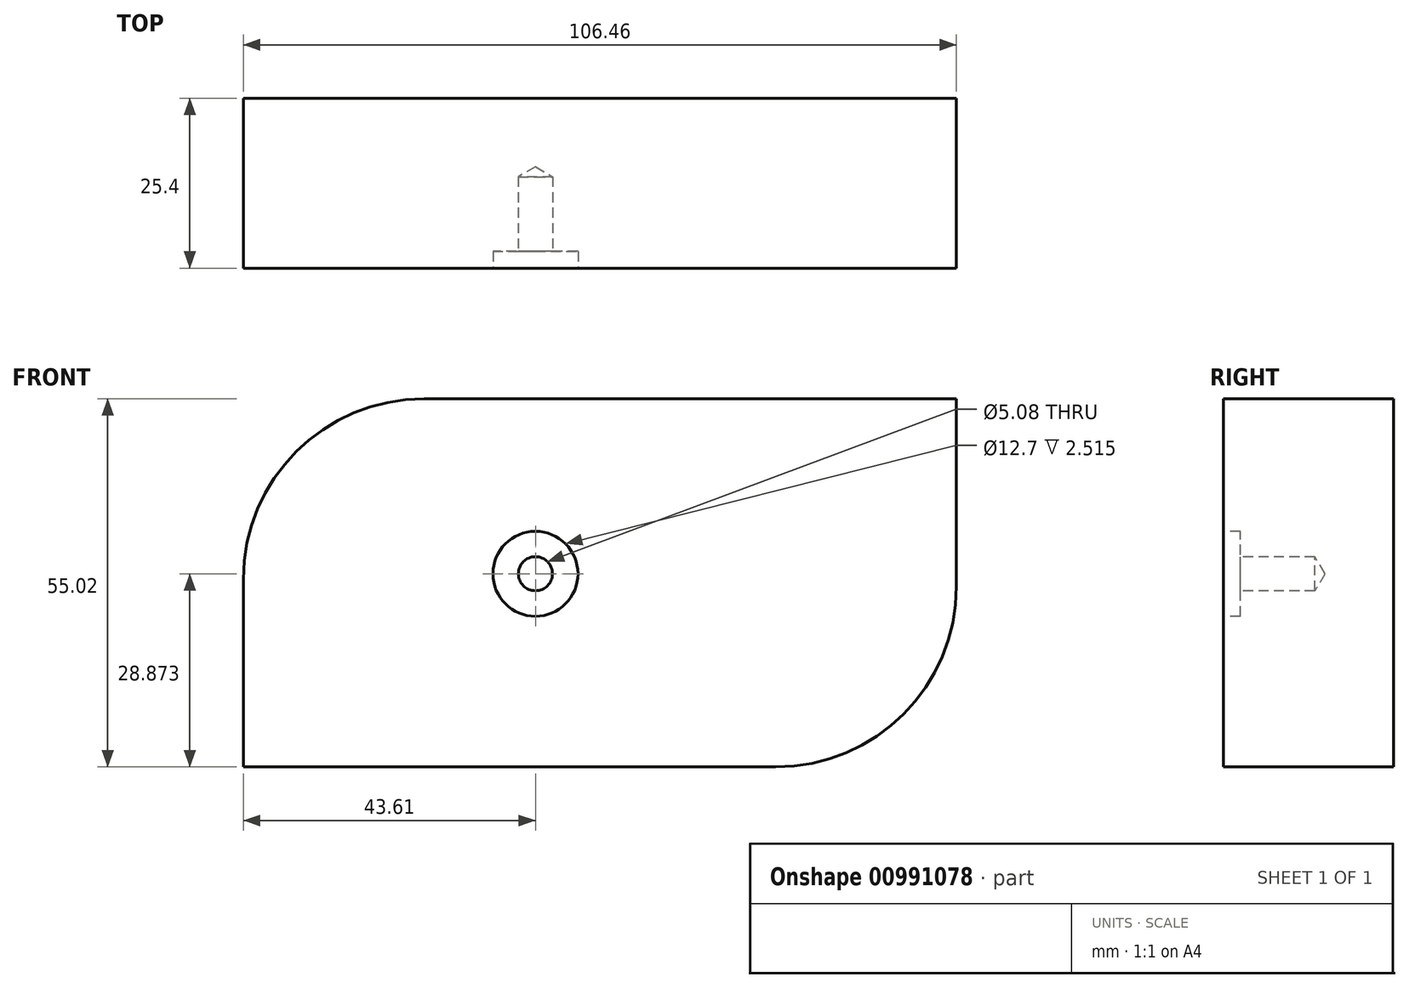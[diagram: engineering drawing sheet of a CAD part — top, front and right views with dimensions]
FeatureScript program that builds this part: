
annotation { "Feature Type Name" : "Feature", "Feature Type Description" : "" }
export const myFeature = defineFeature(function(context is Context, id is Id, definition is map)
    precondition{}
    {
        {
            var Q0;
            Q0=qCreatedBy(makeId("Front.planeOp"),FACE);
            var sketch = newSketch(context, id + "F0", { "sketchPlane" : qUnion([Q0])});
            skLineSegment(sketch, "E0.bottom", {"start": v(-118.7, 34) * mm, "end": v(-12.25, 34) * mm});
            skLineSegment(sketch, "E0.top", {"start": v(-118.7, -21) * mm, "end": v(-12.25, -21) * mm});
            skLineSegment(sketch, "E0.left", {"start": v(-118.7, 34) * mm, "end": v(-118.7, -21) * mm});
            skLineSegment(sketch, "E0.right", {"start": v(-12.25, 34) * mm, "end": v(-12.25, -21) * mm});
            skPoint(sketch, "E1", {"position": v(-75.1, 7.86) * mm});
            skSolve(sketch);
        }
        {
            var Q0;
            Q0 = qSketchRegion(id + "F0", true);
            extrude(context, id + "F1", {"entities" : qUnion([Q0]), "oppositeDirection" : true, "depth" : 25.4 * mm, "offsetDistance" : 25.4 * mm});
        }
        {
            var Q0;
            Q0=makeQuery(id+"F1.opExtrude","SWEPT_EDGE",EDGE,{"disambiguationData":[OSD([sQuery(id+"F0.wireOp",EDGE,"E0.top"),sQuery(id+"F0.wireOp",EDGE,"E0.right")])]});
            var Q1;
            Q1=makeQuery(id+"F1.opExtrude","SWEPT_EDGE",EDGE,{"disambiguationData":[OSD([sQuery(id+"F0.wireOp",EDGE,"E0.bottom"),sQuery(id+"F0.wireOp",EDGE,"E0.left")])]});
            fillet(context, id + "F2", {"entities" : qUnion([Q0, Q1]), "radius" : 26.98 * mm, "tangentPropagation" : true, "allowEdgeOverflow" : false});
        }
        {
            var Q0;
            Q0=sQuery(id+"F0.wireOp",VERTEX,"E1");
            var Q1;
            Q1=makeQuery(id+"F1.opExtrude","SWEPT_BODY",BODY,{"disambiguationData":[OSD([sQuery(id+"F0.wireOp",EDGE,"E0.bottom"),sQuery(id+"F0.wireOp",EDGE,"E0.top"),sQuery(id+"F0.wireOp",EDGE,"E0.left"),sQuery(id+"F0.wireOp",EDGE,"E0.right")])]});
            hole(context, id + "F3", {"style" : HoleStyle.C_BORE, "endStyle" : HoleEndStyle.BLIND, "holeDiameter" : 5.08 * mm, "cBoreDiameter" : 12.7 * mm, "cBoreDepth" : 2.5 * mm, "majorDiameter" : 6.35 * mm, "holeDepth" : 13.65 * mm, "isTappedThrough" : true, "tappedDepth" : 12.06 * mm, "tapClearance" : 3, "startFromSketch" : true, "locations" : qUnion([Q0]), "scope" : qUnion([Q1])});
        }
    });
